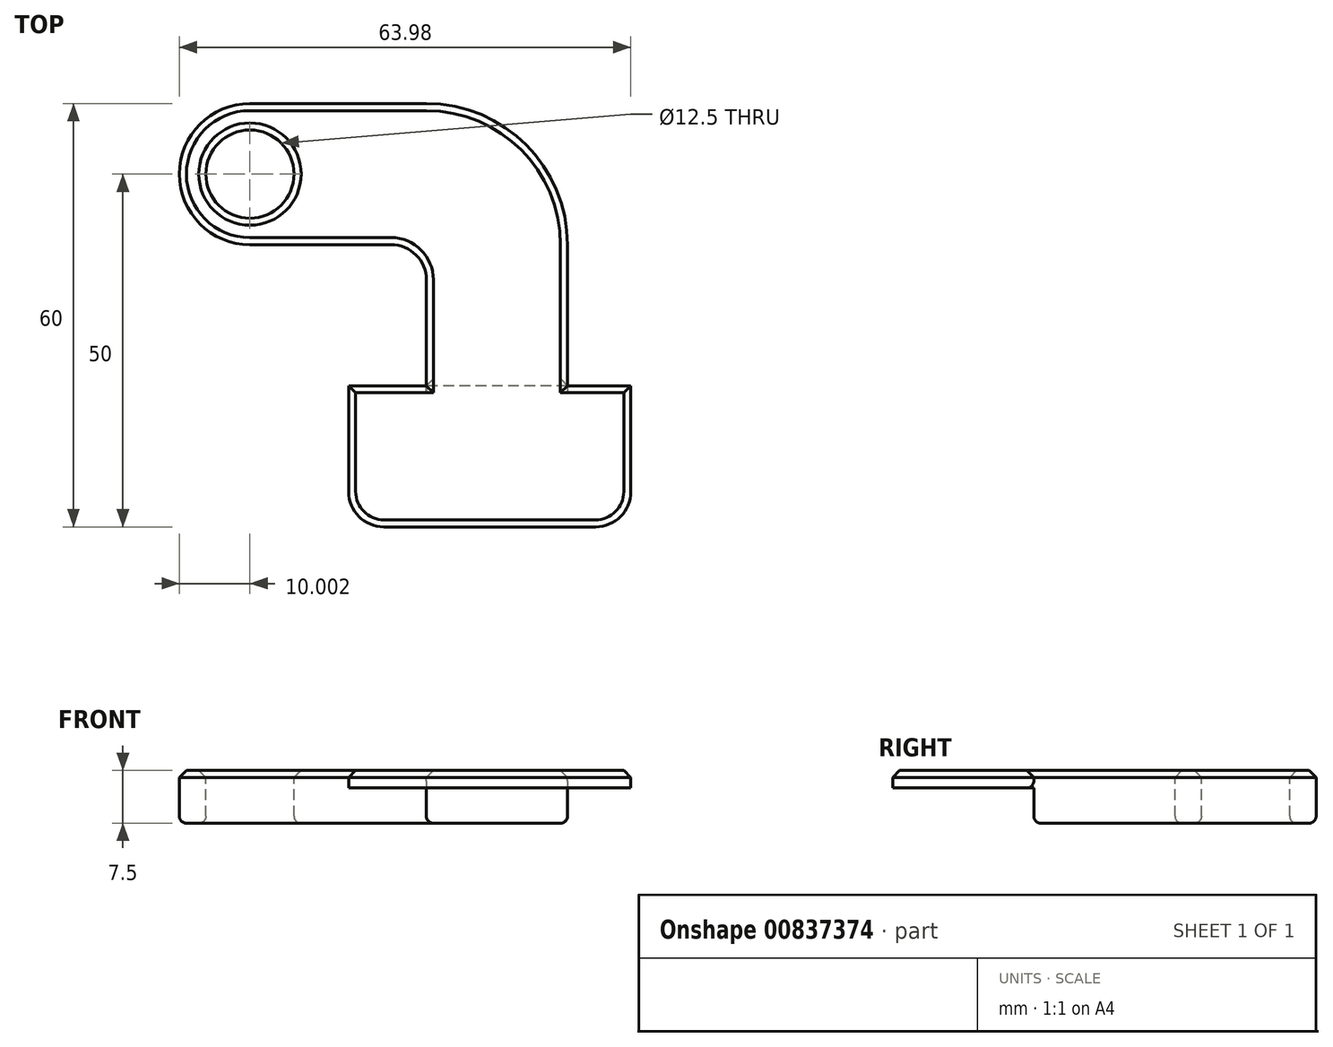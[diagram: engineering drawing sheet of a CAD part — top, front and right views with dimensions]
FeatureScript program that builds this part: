
annotation { "Feature Type Name" : "Feature", "Feature Type Description" : "" }
export const myFeature = defineFeature(function(context is Context, id is Id, definition is map)
    precondition{}
    {
        {
            var Q0;
            Q0=qCreatedBy(makeId("Top.planeOp"),FACE);
            var sketch = newSketch(context, id + "F0", { "sketchPlane" : qUnion([Q0])});
            skCircle(sketch, "E0", {"center": v(-40.26, 0) * mm, "radius": 6.25 * mm});
            skArc(sketch, "E1", {"start": v(-40.26, 10) * mm, "mid": v(-50.26, 0) * mm, "end": v(-40.26, -10) * mm});
            skLineSegment(sketch, "E2.bottom", {"start": v(-40.26, 10) * mm, "end": v(-15.26, 10) * mm});
            skLineSegment(sketch, "E2.top", {"start": v(-40.26, -10) * mm, "end": v(-20.26, -10) * mm});
            skLineSegment(sketch, "E3.top", {"start": v(4.74, -30) * mm, "end": v(-15.26, -30) * mm});
            skLineSegment(sketch, "E3.left", {"start": v(4.74, -10) * mm, "end": v(4.74, -30) * mm});
            skLineSegment(sketch, "E3.right", {"start": v(-15.26, -15) * mm, "end": v(-15.26, -30) * mm});
            skLineSegment(sketch, "E4.bottom", {"start": v(13.72, -30) * mm, "end": v(-26.28, -30) * mm});
            skLineSegment(sketch, "E4.top", {"start": v(8.72, -50) * mm, "end": v(-21.28, -50) * mm});
            skLineSegment(sketch, "E4.left", {"start": v(13.72, -30) * mm, "end": v(13.72, -45) * mm});
            skLineSegment(sketch, "E4.right", {"start": v(-26.28, -30) * mm, "end": v(-26.28, -45) * mm});
            skPoint(sketch, "E5.visualSharp", {"position": v(4.74, 10) * mm});
            skArc(sketch, "E5.filletArc", {"start": v(4.74, -10) * mm, "mid": v(-1.12, 4.14) * mm, "end": v(-15.26, 10) * mm});
            skArc(sketch, "E6.filletArc", {"start": v(-15.26, -15) * mm, "mid": v(-16.72, -11.46) * mm, "end": v(-20.26, -10) * mm});
            skPoint(sketch, "E7.visualSharp", {"position": v(13.72, -50) * mm});
            skArc(sketch, "E7.filletArc", {"start": v(8.72, -50) * mm, "mid": v(12.26, -48.54) * mm, "end": v(13.72, -45) * mm});
            skPoint(sketch, "E8.visualSharp", {"position": v(-26.28, -50) * mm});
            skArc(sketch, "E8.filletArc", {"start": v(-26.28, -45) * mm, "mid": v(-24.81, -48.54) * mm, "end": v(-21.28, -50) * mm});
            skSolve(sketch);
        }
        {
            var Q0;
            Q0=makeQuery(id+"F0.imprint","IMPRINT",FACE,{"disambiguationData":[TD([[makeQuery(id+"F0.imprint","IMPRINT",EDGE,{"derivedFrom":sQuery(id+"F0.wireOp",EDGE,"E0")}),-1.0]])]});
            extrude(context, id + "F1", {"entities" : qUnion([Q0]), "oppositeDirection" : true, "depth" : 7.5 * mm, "offsetDistance" : 25 * mm});
        }
        {
            var Q0;
            {var subQ1=sQuery(id+"F0.wireOp",EDGE,"E3.top");Q0=makeQuery(id+"F0.imprint","IMPRINT",FACE,{"disambiguationData":[TD([[makeQuery(id+"F0.imprint","IMPRINT",EDGE,{"derivedFrom":subQ1}),1.0]])]});}
            extrude(context, id + "F2", {"entities" : qUnion([Q0]), "operationType" : NewBodyOperationType.ADD, "oppositeDirection" : true, "depth" : 2.5 * mm, "offsetDistance" : 25 * mm});
        }
        {
            var Q0;
            Q0=makeQuery(id+"F1.opExtrude","CAP_EDGE",EDGE,{"disambiguationData":[OSD([sQuery(id+"F0.wireOp",EDGE,"E0")])],"isStart":false});
            var Q1;
            Q1=makeQuery(id+"F1.opExtrude","CAP_FACE",FACE,{"disambiguationData":[OSD([sQuery(id+"F0.wireOp",EDGE,"E0"),sQuery(id+"F0.wireOp",EDGE,"E1"),sQuery(id+"F0.wireOp",EDGE,"E2.bottom"),sQuery(id+"F0.wireOp",EDGE,"E2.top"),sQuery(id+"F0.wireOp",EDGE,"E3.top"),sQuery(id+"F0.wireOp",EDGE,"E3.left"),sQuery(id+"F0.wireOp",EDGE,"E3.right"),sQuery(id+"F0.wireOp",EDGE,"E5.filletArc"),sQuery(id+"F0.wireOp",EDGE,"E6.filletArc")])],"isStart":false});
            var Q2;
            {var subQ0=sQuery(id+"F0.wireOp",EDGE,"E3.top");var subQ1=sQuery(id+"F0.wireOp",EDGE,"E4.bottom");Q2=makeQuery(id+"F2.boolean.opBoolean","SPLIT",EDGE,{"disambiguationData":[topologyDisambiguationEdgeConnected([makeQuery(id+"F1.opExtrude","SWEPT_FACE",FACE,{"disambiguationData":[OSD([subQ0])]}),makeQuery(id+"F2.opExtrude","CAP_FACE",FACE,{"disambiguationData":[OSD([subQ0,subQ1,sQuery(id+"F0.wireOp",EDGE,"E4.top"),sQuery(id+"F0.wireOp",EDGE,"E4.left"),sQuery(id+"F0.wireOp",EDGE,"E4.right"),sQuery(id+"F0.wireOp",EDGE,"E7.filletArc"),sQuery(id+"F0.wireOp",EDGE,"E8.filletArc")])],"isStart":false})])],"derivedFrom":makeQuery(id+"F2.opExtrude","CAP_EDGE",EDGE,{"disambiguationData":[OSD([subQ0,subQ1])],"isStart":false})});}
            fillet(context, id + "F3", {"entities" : qUnion([Q0, Q1, Q2]), "radius" : 1 * mm, "tangentPropagation" : true, "allowEdgeOverflow" : false});
        }
        {
            var Q0;
            {var subQ0=sQuery(id+"F0.wireOp",EDGE,"E3.top");Q0=makeQuery(id+"F2.boolean.opBoolean","MERGE",FACE,{"derivedFrom":[makeQuery(id+"F1.opExtrude","CAP_FACE",FACE,{"disambiguationData":[OSD([sQuery(id+"F0.wireOp",EDGE,"E0"),sQuery(id+"F0.wireOp",EDGE,"E1"),sQuery(id+"F0.wireOp",EDGE,"E2.bottom"),sQuery(id+"F0.wireOp",EDGE,"E2.top"),subQ0,sQuery(id+"F0.wireOp",EDGE,"E3.left"),sQuery(id+"F0.wireOp",EDGE,"E3.right"),sQuery(id+"F0.wireOp",EDGE,"E5.filletArc"),sQuery(id+"F0.wireOp",EDGE,"E6.filletArc")])],"isStart":true}),makeQuery(id+"F2.opExtrude","CAP_FACE",FACE,{"disambiguationData":[OSD([subQ0,sQuery(id+"F0.wireOp",EDGE,"E4.bottom"),sQuery(id+"F0.wireOp",EDGE,"E4.top"),sQuery(id+"F0.wireOp",EDGE,"E4.left"),sQuery(id+"F0.wireOp",EDGE,"E4.right"),sQuery(id+"F0.wireOp",EDGE,"E7.filletArc"),sQuery(id+"F0.wireOp",EDGE,"E8.filletArc")])],"isStart":true})]});}
            chamfer(context, id + "F4", {"entities" : qUnion([Q0]), "width" : 1 * mm, "tangentPropagation" : true});
        }
    });
